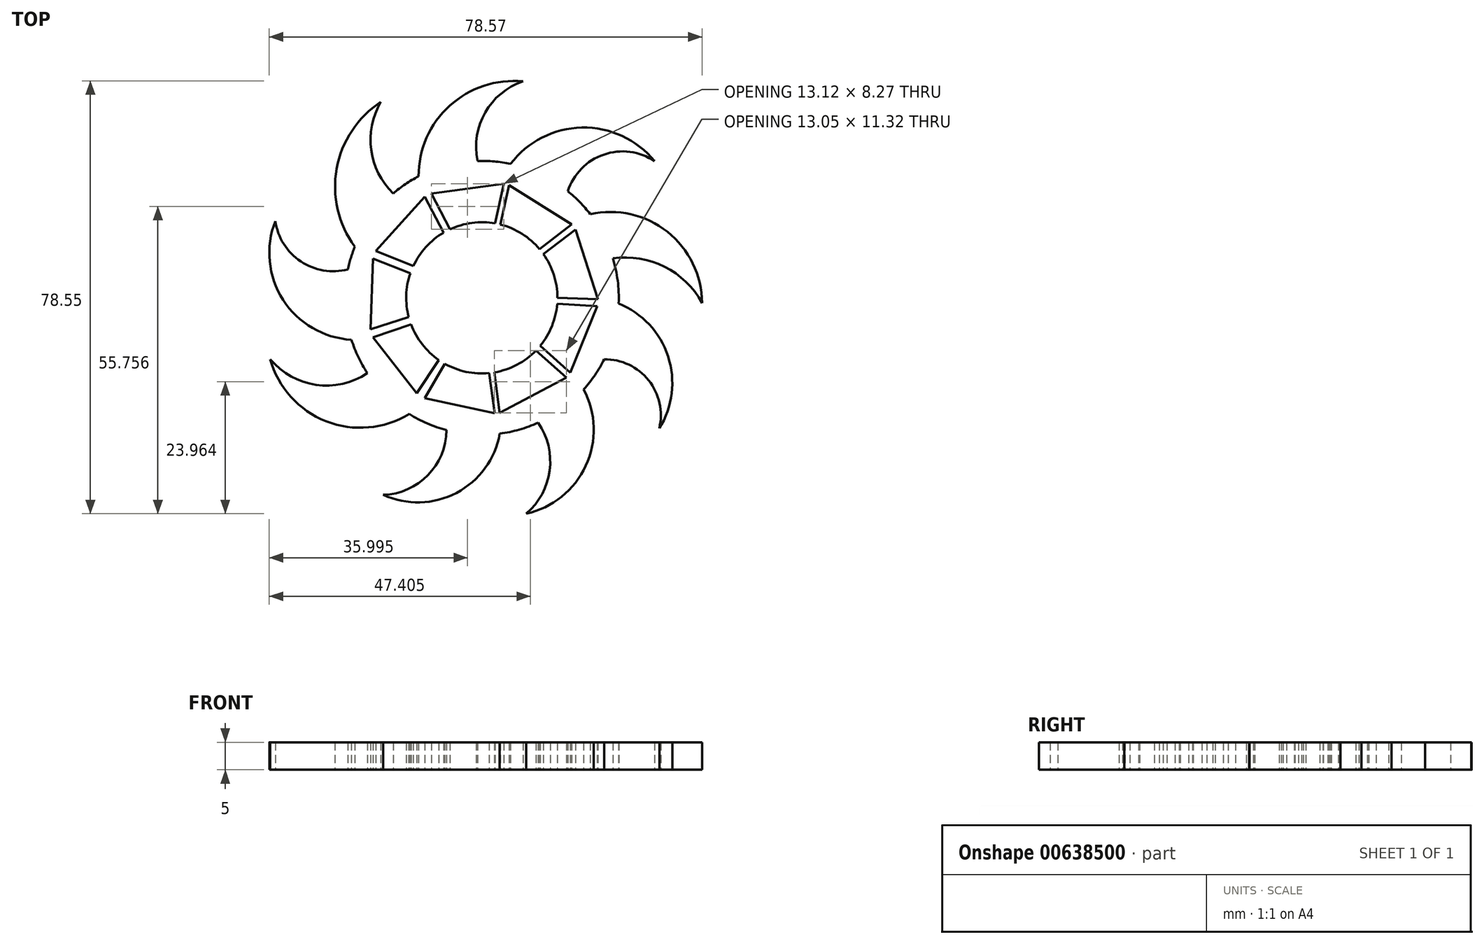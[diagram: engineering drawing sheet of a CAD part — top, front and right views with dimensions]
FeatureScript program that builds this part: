
annotation { "Feature Type Name" : "Feature", "Feature Type Description" : "" }
export const myFeature = defineFeature(function(context is Context, id is Id, definition is map)
    precondition{}
    {
        {
            var Q0;
            Q0=qCreatedBy(makeId("Top.planeOp"),FACE);
            var sketch = newSketch(context, id + "F0", { "sketchPlane" : qUnion([Q0])});
            skPoint(sketch, "E0.0.midPoint", {"position": v(33.83, -33.02) * mm});
            skPoint(sketch, "E1.orphan", {"position": v(28.84, -17.87) * mm});
            skPoint(sketch, "E2.orphan", {"position": v(30.18, -35.52) * mm});
            skPoint(sketch, "E3.orphan", {"position": v(37.49, -30.52) * mm});
            skArc(sketch, "E4", {"start": v(-41.48, -18.75) * mm, "mid": v(-41.64, -19.18) * mm, "end": v(-41.79, -19.61) * mm});
            skCircle(sketch, "E5.cCircle", {"center": v(-3.99, -32.7) * mm, "radius": 19.98 * mm, "construction": true});
            skLineSegment(sketch, "E5.0", {"start": v(-13.92, -13.9) * mm, "end": v(0.48, -11.91) * mm});
            skLineSegment(sketch, "E5.1", {"start": v(0.48, -11.91) * mm, "end": v(12.8, -19.64) * mm});
            skLineSegment(sketch, "E5.2", {"start": v(12.8, -19.64) * mm, "end": v(17.26, -33.49) * mm});
            skLineSegment(sketch, "E5.3", {"start": v(17.26, -33.49) * mm, "end": v(11.78, -46.96) * mm});
            skLineSegment(sketch, "E5.4", {"start": v(11.78, -46.96) * mm, "end": v(-1.08, -53.75) * mm});
            skLineSegment(sketch, "E5.5", {"start": v(-1.08, -53.75) * mm, "end": v(-15.3, -50.7) * mm});
            skLineSegment(sketch, "E5.6", {"start": v(-15.3, -50.7) * mm, "end": v(-24.22, -39.22) * mm});
            skLineSegment(sketch, "E5.7", {"start": v(-24.22, -39.22) * mm, "end": v(-23.68, -24.69) * mm});
            skLineSegment(sketch, "E5.8", {"start": v(-23.68, -24.69) * mm, "end": v(-13.92, -13.9) * mm});
            skPoint(sketch, "E5.0.midPoint", {"position": v(-6.72, -12.9) * mm});
            skCircle(sketch, "E6", {"center": v(-3.99, -32.7) * mm, "radius": 24.86 * mm});
            skLineSegment(sketch, "E7", {"start": v(-3.99, -32.7) * mm, "end": v(-1.1, -19.27) * mm});
            skLineSegment(sketch, "E8", {"start": v(-3.99, -32.7) * mm, "end": v(6.88, -24.31) * mm});
            skLineSegment(sketch, "E9", {"start": v(-3.99, -32.7) * mm, "end": v(-10.32, -20.52) * mm});
            skLineSegment(sketch, "E10", {"start": v(-3.99, -32.7) * mm, "end": v(-16.71, -27.56) * mm});
            skLineSegment(sketch, "E11", {"start": v(-3.99, -32.7) * mm, "end": v(-17.05, -36.9) * mm});
            skLineSegment(sketch, "E12", {"start": v(-3.99, -32.7) * mm, "end": v(-11.26, -44.33) * mm});
            skLineSegment(sketch, "E13", {"start": v(-3.99, -32.7) * mm, "end": v(-2.19, -46.3) * mm});
            skLineSegment(sketch, "E14", {"start": v(-3.99, -32.7) * mm, "end": v(9.73, -33.26) * mm});
            skLineSegment(sketch, "E15", {"start": v(-3.99, -32.7) * mm, "end": v(6.23, -41.87) * mm});
            skArc(sketch, "E16", {"start": v(27.38, -7.87) * mm, "mid": v(14.18, -1.78) * mm, "end": v(1.23, -8.38) * mm});
            skArc(sketch, "E17", {"start": v(27.38, -7.87) * mm, "mid": v(18.14, -6.68) * mm, "end": v(11.62, -13.34) * mm});
            skArc(sketch, "E18", {"start": v(3.48, 6.6) * mm, "mid": v(-9.81, 2.18) * mm, "end": v(-15.46, -10.64) * mm});
            skArc(sketch, "E19", {"start": v(3.48, 6.6) * mm, "mid": v(-3.38, 0.95) * mm, "end": v(-4.73, -7.84) * mm});
            skArc(sketch, "E20", {"start": v(-22.32, 2.86) * mm, "mid": v(-30.34, -9.25) * mm, "end": v(-27.04, -23.4) * mm});
            skArc(sketch, "E21", {"start": v(-22.32, 2.86) * mm, "mid": v(-24.09, -5.83) * mm, "end": v(-20.09, -13.75) * mm});
            skArc(sketch, "E22", {"start": v(-41.48, -18.75) * mm, "mid": v(-40.07, -33.05) * mm, "end": v(-27.66, -40.3) * mm});
            skArc(sketch, "E23", {"start": v(-41.48, -18.75) * mm, "mid": v(-36.85, -26.08) * mm, "end": v(-28.3, -27.53) * mm});
            skArc(sketch, "E24", {"start": v(-42.4, -43.84) * mm, "mid": v(-32.26, -55.1) * mm, "end": v(-17.17, -53.78) * mm});
            skArc(sketch, "E25", {"start": v(-42.4, -43.84) * mm, "mid": v(-34.07, -48.49) * mm, "end": v(-24.76, -46.35) * mm});
            skArc(sketch, "E26", {"start": v(36, -33.63) * mm, "mid": v(29.7, -20.71) * mm, "end": v(15.7, -17.5) * mm});
            skArc(sketch, "E27", {"start": v(36, -33.63) * mm, "mid": v(29.18, -27.04) * mm, "end": v(19.82, -25.54) * mm});
            skArc(sketch, "E28", {"start": v(28.24, -56.39) * mm, "mid": v(29.83, -43.33) * mm, "end": v(20.86, -33.72) * mm});
            skArc(sketch, "E29", {"start": v(28.24, -56.39) * mm, "mid": v(26.3, -47.67) * mm, "end": v(18.24, -43.84) * mm});
            skArc(sketch, "E30", {"start": v(4.08, -71.87) * mm, "mid": v(14.9, -63.18) * mm, "end": v(14.51, -49.3) * mm});
            skArc(sketch, "E31", {"start": v(4.08, -71.87) * mm, "mid": v(8.33, -64.03) * mm, "end": v(6.23, -55.36) * mm});
            skArc(sketch, "E32", {"start": v(-21.9, -68.46) * mm, "mid": v(-8.59, -68.1) * mm, "end": v(-0.73, -57.34) * mm});
            skArc(sketch, "E33", {"start": v(-21.9, -68.46) * mm, "mid": v(-13.79, -64.9) * mm, "end": v(-10.4, -56.72) * mm});
            skArc(sketch, "E34.trimOffspring", {"start": v(-42.4, -43.84) * mm, "mid": v(-42.3, -44.16) * mm, "end": v(-42.2, -44.48) * mm});
            skCircle(sketch, "E35", {"center": v(-3.99, -32.7) * mm, "radius": 13.73 * mm});
            skLineSegment(sketch, "E36", {"start": v(0, -11.91) * mm, "end": v(-1.56, -19.19) * mm});
            skLineSegment(sketch, "E37", {"start": v(0.99, -12.23) * mm, "end": v(-0.6, -19.4) * mm});
            skLineSegment(sketch, "E38.trimOffspring", {"start": v(0.47, -11.91) * mm, "end": v(1.23, -8.38) * mm});
            skLineSegment(sketch, "E39", {"start": v(-14.31, -14.33) * mm, "end": v(-10.92, -20.85) * mm});
            skLineSegment(sketch, "E40", {"start": v(-13.14, -13.8) * mm, "end": v(-9.78, -20.25) * mm});
            skLineSegment(sketch, "E41.trimOffspring", {"start": v(-13.78, -13.88) * mm, "end": v(-15.46, -10.64) * mm});
            skLineSegment(sketch, "E42", {"start": v(-23.22, -24.18) * mm, "end": v(-16.44, -26.92) * mm});
            skLineSegment(sketch, "E43", {"start": v(-23.71, -25.54) * mm, "end": v(-16.98, -28.26) * mm});
            skLineSegment(sketch, "E44.trimOffspring", {"start": v(-23.68, -24.75) * mm, "end": v(-27.04, -23.4) * mm});
            skLineSegment(sketch, "E45", {"start": v(-24.2, -38.42) * mm, "end": v(-17.26, -36.2) * mm});
            skLineSegment(sketch, "E46", {"start": v(-23.71, -39.87) * mm, "end": v(-16.83, -37.53) * mm});
            skLineSegment(sketch, "E47.trimOffspring", {"start": v(-24.22, -39.2) * mm, "end": v(-27.66, -40.3) * mm});
            skLineSegment(sketch, "E48", {"start": v(-11.82, -43.96) * mm, "end": v(-15.82, -50.02) * mm});
            skLineSegment(sketch, "E49", {"start": v(-14.34, -50.9) * mm, "end": v(-10.7, -44.67) * mm});
            skLineSegment(sketch, "E50.trimOffspring", {"start": v(-15.25, -50.7) * mm, "end": v(-17.17, -53.78) * mm});
            skLineSegment(sketch, "E51", {"start": v(-1.7, -46.23) * mm, "end": v(-0.72, -53.57) * mm});
            skLineSegment(sketch, "E52", {"start": v(-2.7, -46.36) * mm, "end": v(-1.66, -53.63) * mm});
            skLineSegment(sketch, "E53", {"start": v(5.87, -42.25) * mm, "end": v(11.36, -47.18) * mm});
            skLineSegment(sketch, "E54", {"start": v(6.64, -41.38) * mm, "end": v(12.05, -46.3) * mm});
            skLineSegment(sketch, "E55.trimOffspring", {"start": v(11.8, -46.88) * mm, "end": v(14.51, -49.3) * mm});
            skLineSegment(sketch, "E56.trimOffspring", {"start": v(-1.2, -53.73) * mm, "end": v(-0.73, -57.34) * mm});
            skLineSegment(sketch, "E57", {"start": v(9.74, -32.67) * mm, "end": v(17.08, -32.94) * mm});
            skLineSegment(sketch, "E58", {"start": v(9.7, -33.8) * mm, "end": v(16.97, -34.19) * mm});
            skLineSegment(sketch, "E59", {"start": v(6.51, -23.86) * mm, "end": v(12.34, -19.36) * mm});
            skLineSegment(sketch, "E60", {"start": v(7.2, -24.74) * mm, "end": v(13.01, -20.32) * mm});
            skLineSegment(sketch, "E61.trimOffspring", {"start": v(17.22, -33.57) * mm, "end": v(20.86, -33.72) * mm});
            skLineSegment(sketch, "E62.trimOffspring", {"start": v(12.82, -19.73) * mm, "end": v(15.7, -17.5) * mm});
            skSolve(sketch);
        }
        {
            var Q0;
            {var subQ3=sQuery(id+"F0.wireOp",EDGE,"E61.trimOffspring");Q0=makeQuery(id+"F0.imprint","IMPRINT",FACE,{"disambiguationData":[TD([[makeQuery(id+"F0.imprint","IMPRINT",EDGE,{"derivedFrom":subQ3}),1.0]])]});}
            var Q1;
            {var subQ2=sQuery(id+"F0.wireOp",EDGE,"E48");Q1=makeQuery(id+"F0.imprint","IMPRINT",FACE,{"disambiguationData":[TD([[makeQuery(id+"F0.imprint","IMPRINT",EDGE,{"derivedFrom":subQ2}),1.0]])]});}
            var Q2;
            {var subQ3=sQuery(id+"F0.wireOp",EDGE,"E12");Q2=makeQuery(id+"F0.imprint","IMPRINT",FACE,{"disambiguationData":[TD([[makeQuery(id+"F0.imprint","IMPRINT",EDGE,{"derivedFrom":subQ3}),1.0]])]});}
            var Q3;
            {var subQ3=sQuery(id+"F0.wireOp",EDGE,"E7");Q3=makeQuery(id+"F0.imprint","IMPRINT",FACE,{"disambiguationData":[TD([[makeQuery(id+"F0.imprint","IMPRINT",EDGE,{"derivedFrom":subQ3}),-1.0]])]});}
            var Q4;
            {var subQ0=sQuery(id+"F0.wireOp",EDGE,"E44.trimOffspring");Q4=makeQuery(id+"F0.imprint","IMPRINT",FACE,{"disambiguationData":[TD([[makeQuery(id+"F0.imprint","IMPRINT",EDGE,{"derivedFrom":subQ0}),1.0]])]});}
            var Q5;
            {var subQ7=sQuery(id+"F0.wireOp",EDGE,"E39");Q5=makeQuery(id+"F0.imprint","IMPRINT",FACE,{"disambiguationData":[TD([[makeQuery(id+"F0.imprint","IMPRINT",EDGE,{"derivedFrom":subQ7}),1.0]])]});}
            var Q6;
            {var subQ10=sQuery(id+"F0.wireOp",EDGE,"E47.trimOffspring");Q6=makeQuery(id+"F0.imprint","IMPRINT",FACE,{"disambiguationData":[TD([[makeQuery(id+"F0.imprint","IMPRINT",EDGE,{"derivedFrom":subQ10}),1.0]])]});}
            var Q7;
            {var subQ1=sQuery(id+"F0.wireOp",EDGE,"E13");Q7=makeQuery(id+"F0.imprint","IMPRINT",FACE,{"disambiguationData":[TD([[makeQuery(id+"F0.imprint","IMPRINT",EDGE,{"derivedFrom":subQ1}),1.0]])]});}
            var Q8;
            {var subQ4=sQuery(id+"F0.wireOp",EDGE,"E7");Q8=makeQuery(id+"F0.imprint","IMPRINT",FACE,{"disambiguationData":[TD([[makeQuery(id+"F0.imprint","IMPRINT",EDGE,{"derivedFrom":subQ4}),1.0]])]});}
            var Q9;
            {var subQ2=sQuery(id+"F0.wireOp",EDGE,"E42");Q9=makeQuery(id+"F0.imprint","IMPRINT",FACE,{"disambiguationData":[TD([[makeQuery(id+"F0.imprint","IMPRINT",EDGE,{"derivedFrom":subQ2}),-1.0]])]});}
            var Q10;
            {var subQ7=sQuery(id+"F0.wireOp",EDGE,"E41.trimOffspring");Q10=makeQuery(id+"F0.imprint","IMPRINT",FACE,{"disambiguationData":[TD([[makeQuery(id+"F0.imprint","IMPRINT",EDGE,{"derivedFrom":subQ7}),1.0]])]});}
            var Q11;
            {var subQ2=sQuery(id+"F0.wireOp",EDGE,"E55.trimOffspring");Q11=makeQuery(id+"F0.imprint","IMPRINT",FACE,{"disambiguationData":[TD([[makeQuery(id+"F0.imprint","IMPRINT",EDGE,{"derivedFrom":subQ2}),1.0]])]});}
            var Q12;
            {var subQ0=sQuery(id+"F0.wireOp",EDGE,"E45");Q12=makeQuery(id+"F0.imprint","IMPRINT",FACE,{"disambiguationData":[TD([[makeQuery(id+"F0.imprint","IMPRINT",EDGE,{"derivedFrom":subQ0}),-1.0]])]});}
            var Q13;
            {var subQ4=sQuery(id+"F0.wireOp",EDGE,"E14");Q13=makeQuery(id+"F0.imprint","IMPRINT",FACE,{"disambiguationData":[TD([[makeQuery(id+"F0.imprint","IMPRINT",EDGE,{"derivedFrom":subQ4}),-1.0]])]});}
            var Q14;
            {var subQ3=sQuery(id+"F0.wireOp",EDGE,"E53");Q14=makeQuery(id+"F0.imprint","IMPRINT",FACE,{"disambiguationData":[TD([[makeQuery(id+"F0.imprint","IMPRINT",EDGE,{"derivedFrom":subQ3}),1.0]])]});}
            var Q15;
            {var subQ4=sQuery(id+"F0.wireOp",EDGE,"E8");Q15=makeQuery(id+"F0.imprint","IMPRINT",FACE,{"disambiguationData":[TD([[makeQuery(id+"F0.imprint","IMPRINT",EDGE,{"derivedFrom":subQ4}),-1.0]])]});}
            var Q16;
            {var subQ0=sQuery(id+"F0.wireOp",EDGE,"E26");Q16=makeQuery(id+"F0.imprint","IMPRINT",FACE,{"disambiguationData":[TD([[makeQuery(id+"F0.imprint","IMPRINT",EDGE,{"derivedFrom":subQ0}),1.0]])]});}
            var Q17;
            {var subQ0=sQuery(id+"F0.wireOp",EDGE,"E16");Q17=makeQuery(id+"F0.imprint","IMPRINT",FACE,{"disambiguationData":[TD([[makeQuery(id+"F0.imprint","IMPRINT",EDGE,{"derivedFrom":subQ0}),1.0]])]});}
            var Q18;
            {var subQ0=sQuery(id+"F0.wireOp",EDGE,"E18");Q18=makeQuery(id+"F0.imprint","IMPRINT",FACE,{"disambiguationData":[TD([[makeQuery(id+"F0.imprint","IMPRINT",EDGE,{"derivedFrom":subQ0}),1.0]])]});}
            var Q19;
            {var subQ0=sQuery(id+"F0.wireOp",EDGE,"E20");Q19=makeQuery(id+"F0.imprint","IMPRINT",FACE,{"disambiguationData":[TD([[makeQuery(id+"F0.imprint","IMPRINT",EDGE,{"derivedFrom":subQ0}),1.0]])]});}
            var Q20;
            {var subQ0=sQuery(id+"F0.wireOp",EDGE,"E32");Q20=makeQuery(id+"F0.imprint","IMPRINT",FACE,{"disambiguationData":[TD([[makeQuery(id+"F0.imprint","IMPRINT",EDGE,{"derivedFrom":subQ0}),1.0]])]});}
            var Q21;
            {var subQ0=sQuery(id+"F0.wireOp",EDGE,"E30");Q21=makeQuery(id+"F0.imprint","IMPRINT",FACE,{"disambiguationData":[TD([[makeQuery(id+"F0.imprint","IMPRINT",EDGE,{"derivedFrom":subQ0}),1.0]])]});}
            var Q22;
            {var subQ0=sQuery(id+"F0.wireOp",EDGE,"E28");Q22=makeQuery(id+"F0.imprint","IMPRINT",FACE,{"disambiguationData":[TD([[makeQuery(id+"F0.imprint","IMPRINT",EDGE,{"derivedFrom":subQ0}),1.0]])]});}
            var Q23;
            {var subQ0=sQuery(id+"F0.wireOp",EDGE,"E4");Q23=makeQuery(id+"F0.imprint","IMPRINT",FACE,{"disambiguationData":[TD([[makeQuery(id+"F0.imprint","IMPRINT",EDGE,{"derivedFrom":subQ0}),1.0]])]});}
            var Q24;
            {var subQ3=sQuery(id+"F0.wireOp",EDGE,"E25");Q24=makeQuery(id+"F0.imprint","IMPRINT",FACE,{"disambiguationData":[TD([[makeQuery(id+"F0.imprint","IMPRINT",EDGE,{"derivedFrom":subQ3}),-1.0]])]});}
            var Q25;
            {var subQ7=sQuery(id+"F0.wireOp",EDGE,"E55.trimOffspring");Q25=makeQuery(id+"F0.imprint","IMPRINT",FACE,{"disambiguationData":[TD([[makeQuery(id+"F0.imprint","IMPRINT",EDGE,{"derivedFrom":subQ7}),-1.0]])]});}
            var Q26;
            {var subQ3=sQuery(id+"F0.wireOp",EDGE,"E9");Q26=makeQuery(id+"F0.imprint","IMPRINT",FACE,{"disambiguationData":[TD([[makeQuery(id+"F0.imprint","IMPRINT",EDGE,{"derivedFrom":subQ3}),1.0]])]});}
            var Q27;
            {var subQ7=sQuery(id+"F0.wireOp",EDGE,"E38.trimOffspring");Q27=makeQuery(id+"F0.imprint","IMPRINT",FACE,{"disambiguationData":[TD([[makeQuery(id+"F0.imprint","IMPRINT",EDGE,{"derivedFrom":subQ7}),-1.0]])]});}
            var Q28;
            {var subQ3=sQuery(id+"F0.wireOp",EDGE,"E10");Q28=makeQuery(id+"F0.imprint","IMPRINT",FACE,{"disambiguationData":[TD([[makeQuery(id+"F0.imprint","IMPRINT",EDGE,{"derivedFrom":subQ3}),1.0]])]});}
            var Q29;
            {var subQ7=sQuery(id+"F0.wireOp",EDGE,"E59");Q29=makeQuery(id+"F0.imprint","IMPRINT",FACE,{"disambiguationData":[TD([[makeQuery(id+"F0.imprint","IMPRINT",EDGE,{"derivedFrom":subQ7}),-1.0]])]});}
            var Q30;
            {var subQ0=sQuery(id+"F0.wireOp",EDGE,"E38.trimOffspring");Q30=makeQuery(id+"F0.imprint","IMPRINT",FACE,{"disambiguationData":[TD([[makeQuery(id+"F0.imprint","IMPRINT",EDGE,{"derivedFrom":subQ0}),1.0]])]});}
            var Q31;
            {var subQ2=sQuery(id+"F0.wireOp",EDGE,"E50.trimOffspring");Q31=makeQuery(id+"F0.imprint","IMPRINT",FACE,{"disambiguationData":[TD([[makeQuery(id+"F0.imprint","IMPRINT",EDGE,{"derivedFrom":subQ2}),1.0]])]});}
            var Q32;
            {var subQ4=sQuery(id+"F0.wireOp",EDGE,"E11");Q32=makeQuery(id+"F0.imprint","IMPRINT",FACE,{"disambiguationData":[TD([[makeQuery(id+"F0.imprint","IMPRINT",EDGE,{"derivedFrom":subQ4}),1.0]])]});}
            var Q33;
            {var subQ7=sQuery(id+"F0.wireOp",EDGE,"E57");Q33=makeQuery(id+"F0.imprint","IMPRINT",FACE,{"disambiguationData":[TD([[makeQuery(id+"F0.imprint","IMPRINT",EDGE,{"derivedFrom":subQ7}),-1.0]])]});}
            var Q34;
            {var subQ3=sQuery(id+"F0.wireOp",EDGE,"E37");Q34=makeQuery(id+"F0.imprint","IMPRINT",FACE,{"disambiguationData":[TD([[makeQuery(id+"F0.imprint","IMPRINT",EDGE,{"derivedFrom":subQ3}),-1.0]])]});}
            var Q35;
            {var subQ7=sQuery(id+"F0.wireOp",EDGE,"E51");Q35=makeQuery(id+"F0.imprint","IMPRINT",FACE,{"disambiguationData":[TD([[makeQuery(id+"F0.imprint","IMPRINT",EDGE,{"derivedFrom":subQ7}),-1.0]])]});}
            var Q36;
            {var subQ0=sQuery(id+"F0.wireOp",EDGE,"E4");Q36=makeQuery(id+"F0.imprint","IMPRINT",FACE,{"disambiguationData":[TD([[makeQuery(id+"F0.imprint","IMPRINT",EDGE,{"derivedFrom":subQ0}),-1.0]])]});}
            var Q37;
            {var subQ0=sQuery(id+"F0.wireOp",EDGE,"E34.trimOffspring");Q37=makeQuery(id+"F0.imprint","IMPRINT",FACE,{"disambiguationData":[TD([[makeQuery(id+"F0.imprint","IMPRINT",EDGE,{"derivedFrom":subQ0}),-1.0]])]});}
            extrude(context, id + "F1", {"entities" : qUnion([Q0, Q1, Q2, Q3, Q4, Q5, Q6, Q7, Q8, Q9, Q10, Q11, Q12, Q13, Q14, Q15, Q16, Q17, Q18, Q19, Q20, Q21, Q22, Q23, Q24, Q25, Q26, Q27, Q28, Q29, Q30, Q31, Q32, Q33, Q34, Q35, Q36, Q37]), "depth" : 5 * mm, "offsetDistance" : 25 * mm});
        }
    });
